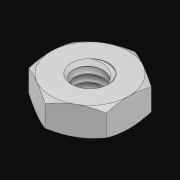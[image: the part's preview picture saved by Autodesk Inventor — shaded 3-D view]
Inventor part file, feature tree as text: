
AUTODESK INVENTOR PART (.ipt)
format: ipt  version: 2021 (Build 250183000, 183)  size: 294,912 bytes
history: native  units: in
note: dims shown in document units (in); Inventor stores cm internally (conversion verified against a paired STEP export)
features: sketch x1, other x1, mirror x1, extrude x1
ambient origin geometry x8: Origin, YZ Plane, XZ Plane, XY Plane, X Axis, Y Axis, Z Axis, Center Point
bodies: Solid1 (feature_tree)
feature tree (4):
  sketch  "Sketch1"  dims[d0=0.001in d1=0.125in d2=0.0in]
  other  "Srf1"
  mirror  "Mirror1"
  extrude  "ExtrusionSrf1"  Depth=0.125in TaperAngle=0.0deg
